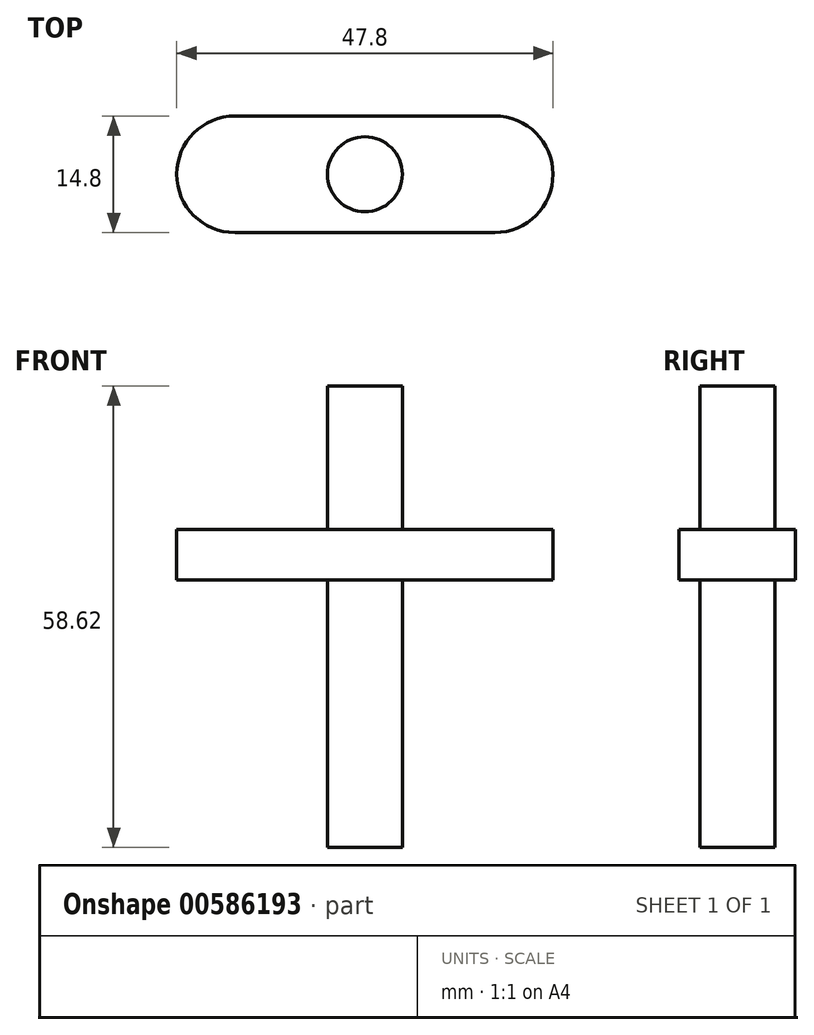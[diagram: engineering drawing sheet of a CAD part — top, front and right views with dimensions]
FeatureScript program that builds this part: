
annotation { "Feature Type Name" : "Feature", "Feature Type Description" : "" }
export const myFeature = defineFeature(function(context is Context, id is Id, definition is map)
    precondition{}
    {
        {
            var Q0;
            Q0=qCreatedBy(makeId("Top.planeOp"),FACE);
            var sketch = newSketch(context, id + "F0", { "sketchPlane" : qUnion([Q0])});
            skArc(sketch, "E0", {"start": v(-16.5, 7.4) * mm, "mid": v(-23.9, 0) * mm, "end": v(-16.5, -7.4) * mm});
            skLineSegment(sketch, "E1", {"start": v(-16.5, 7.4) * mm, "end": v(16.5, 7.4) * mm});
            skLineSegment(sketch, "E2", {"start": v(-16.5, -7.4) * mm, "end": v(16.5, -7.4) * mm});
            skArc(sketch, "E3", {"start": v(16.5, -7.4) * mm, "mid": v(23.9, 0) * mm, "end": v(16.5, 7.4) * mm});
            skPoint(sketch, "E3.centerSnap0", {"position": v(-20.7, 0) * mm});
            skLineSegment(sketch, "E4", {"start": v(-16.5, 0) * mm, "end": v(-23.9, 0) * mm, "construction": true});
            skLineSegment(sketch, "E5", {"start": v(0, 0) * mm, "end": v(23.9, 0) * mm, "construction": true});
            skSolve(sketch);
        }
        {
            var Q0;
            Q0=qSketchRegion(id+"F0",true);
            extrude(context, id + "F1", {"entities" : qUnion([Q0]), "depth" : 6.42 * mm, "offsetDistance" : 25 * mm});
        }
        {
            var Q0;
            Q0=makeQuery(id+"F1.opExtrude","CAP_FACE",FACE,{"disambiguationData":[OSD([sQuery(id+"F0.wireOp",EDGE,"E0"),sQuery(id+"F0.wireOp",EDGE,"E1"),sQuery(id+"F0.wireOp",EDGE,"E2"),sQuery(id+"F0.wireOp",EDGE,"E3")])],"isStart":true});
            var sketch = newSketch(context, id + "F2", { "sketchPlane" : qUnion([Q0])});
            skCircle(sketch, "E6", {"center": v(0, 0) * mm, "radius": 4.76 * mm});
            skSolve(sketch);
        }
        {
            var Q0;
            Q0=qSketchRegion(id+"F2",true);
            extrude(context, id + "F3", {"entities" : qUnion([Q0]), "operationType" : NewBodyOperationType.ADD, "depth" : 34 * mm, "offsetDistance" : 25 * mm});
        }
        {
            var Q0;
            Q0=makeQuery(id+"F1.opExtrude","CAP_FACE",FACE,{"disambiguationData":[OSD([sQuery(id+"F0.wireOp",EDGE,"E0"),sQuery(id+"F0.wireOp",EDGE,"E1"),sQuery(id+"F0.wireOp",EDGE,"E2"),sQuery(id+"F0.wireOp",EDGE,"E3")])],"isStart":false});
            var sketch = newSketch(context, id + "F4", { "sketchPlane" : qUnion([Q0])});
            skCircle(sketch, "E7", {"center": v(0, 0) * mm, "radius": 4.76 * mm});
            skSolve(sketch);
        }
        {
            var Q0;
            Q0=makeQuery(id+"F4.imprint","IMPRINT",FACE,{"disambiguationData":[TD([[makeQuery(id+"F4.imprint","IMPRINT",EDGE,{"derivedFrom":sQuery(id+"F4.wireOp",EDGE,"E7")}),1.0]])]});
            extrude(context, id + "F5", {"entities" : qUnion([Q0]), "operationType" : NewBodyOperationType.ADD, "depth" : 18.2 * mm, "offsetDistance" : 25 * mm});
        }
        {
            var Q0;
            Q0=makeQuery(id+"F5.opExtrude","CAP_FACE",FACE,{"disambiguationData":[OSD([sQuery(id+"F4.wireOp",EDGE,"E7")])],"isStart":false});
            var sketch = newSketch(context, id + "F6", { "sketchPlane" : qUnion([Q0])});
            skLineSegment(sketch, "E8", {"start": v(0, -4.76) * mm, "end": v(0, -3.48) * mm});
            skLineSegment(sketch, "E9", {"start": v(0, -3.48) * mm, "end": v(-3.25, -3.48) * mm});
            skLineSegment(sketch, "E10", {"start": v(-3.25, -3.48) * mm, "end": v(3.25, -3.48) * mm});
            skArc(sketch, "E11", {"start": v(3.25, -3.48) * mm, "mid": v(0, -4.76) * mm, "end": v(-3.25, -3.48) * mm});
            skSolve(sketch);
        }
        {
            var Q0;
            {var subQ0=sQuery(id+"F6.wireOp",EDGE,"E8");Q0=makeQuery(id+"F6.imprint","IMPRINT",FACE,{"disambiguationData":[TD([[makeQuery(id+"F6.imprint","IMPRINT",EDGE,{"derivedFrom":subQ0}),1.0]])]});}
            var Q1;
            {var subQ0=sQuery(id+"F6.wireOp",EDGE,"E8");Q1=makeQuery(id+"F6.imprint","IMPRINT",FACE,{"disambiguationData":[TD([[makeQuery(id+"F6.imprint","IMPRINT",EDGE,{"derivedFrom":subQ0}),-1.0]])]});}
            extrude(context, id + "F7", {"entities" : qUnion([Q0, Q1]), "operationType" : NewBodyOperationType.ADD, "oppositeDirection" : true, "depth" : 18.2 * mm, "offsetDistance" : 25 * mm});
        }
    });
